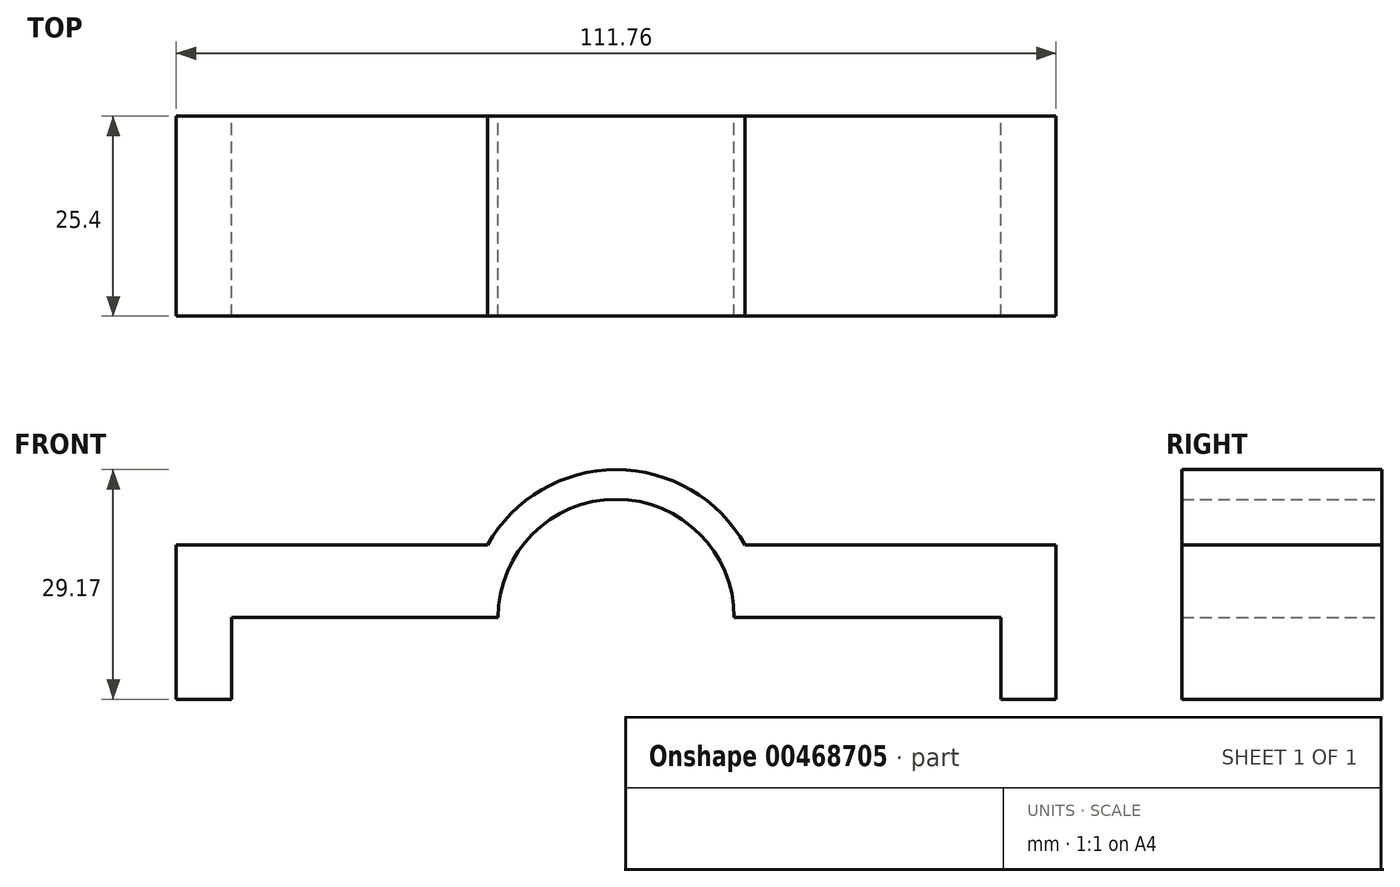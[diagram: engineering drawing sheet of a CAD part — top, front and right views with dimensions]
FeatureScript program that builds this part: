
annotation { "Feature Type Name" : "Feature", "Feature Type Description" : "" }
export const myFeature = defineFeature(function(context is Context, id is Id, definition is map)
    precondition{}
    {
        {
            var Q0;
            Q0=qCreatedBy(makeId("Front.planeOp"),FACE);
            var sketch = newSketch(context, id + "F0", { "sketchPlane" : qUnion([Q0])});
            skArc(sketch, "E0", {"start": v(15, 0) * mm, "mid": v(0, 15) * mm, "end": v(-15, 0) * mm});
            skArc(sketch, "E1", {"start": v(18.76, 0) * mm, "mid": v(0, 18.76) * mm, "end": v(-18.76, 0) * mm});
            skLineSegment(sketch, "E2", {"start": v(-55.88, -10.4) * mm, "end": v(-48.88, -10.4) * mm});
            skLineSegment(sketch, "E3", {"start": v(-48.88, -10.4) * mm, "end": v(-48.88, 0) * mm});
            skPoint(sketch, "E4.orphan", {"position": v(0, 15) * mm});
            skLineSegment(sketch, "E5", {"start": v(-48.88, 0) * mm, "end": v(-15, 0) * mm});
            skLineSegment(sketch, "E6", {"start": v(-16.37, 9.18) * mm, "end": v(-55.88, 9.18) * mm});
            skLineSegment(sketch, "E7", {"start": v(-55.88, 9.18) * mm, "end": v(-55.88, -10.4) * mm});
            skLineSegment(sketch, "E8.MirrorCS", {"start": v(16.37, 9.18) * mm, "end": v(55.88, 9.18) * mm});
            skLineSegment(sketch, "E9.MirrorCS", {"start": v(48.88, 0) * mm, "end": v(15, 0) * mm});
            skLineSegment(sketch, "E10.MirrorCS", {"start": v(48.88, -10.4) * mm, "end": v(48.88, 0) * mm});
            skLineSegment(sketch, "E11.MirrorCS", {"start": v(55.88, 9.18) * mm, "end": v(55.88, -10.4) * mm});
            skLineSegment(sketch, "E12.MirrorCS", {"start": v(55.88, -10.4) * mm, "end": v(48.88, -10.4) * mm});
            skSolve(sketch);
        }
        {
            var Q0;
            Q0=makeQuery(id+"F0.imprint","IMPRINT",FACE,{"disambiguationData":[TD([[makeQuery(id+"F0.imprint","IMPRINT",EDGE,{"derivedFrom":sQuery(id+"F0.wireOp",EDGE,"E2")}),1.0]])]});
            var Q1;
            {var subQ7=sQuery(id+"F0.wireOp",EDGE,"E0");Q1=makeQuery(id+"F0.imprint","IMPRINT",FACE,{"disambiguationData":[TD([[makeQuery(id+"F0.imprint","IMPRINT",EDGE,{"derivedFrom":subQ7}),-1.0]])]});}
            var Q2;
            {var subQ1=sQuery(id+"F0.wireOp",EDGE,"E8.MirrorCS");Q2=makeQuery(id+"F0.imprint","IMPRINT",FACE,{"disambiguationData":[TD([[makeQuery(id+"F0.imprint","IMPRINT",EDGE,{"derivedFrom":subQ1}),-1.0]])]});}
            extrude(context, id + "F1", {"entities" : qUnion([Q0, Q1, Q2]), "endBound" : BoundingType.SYMMETRIC, "depth" : 25.4 * mm});
        }
    });
